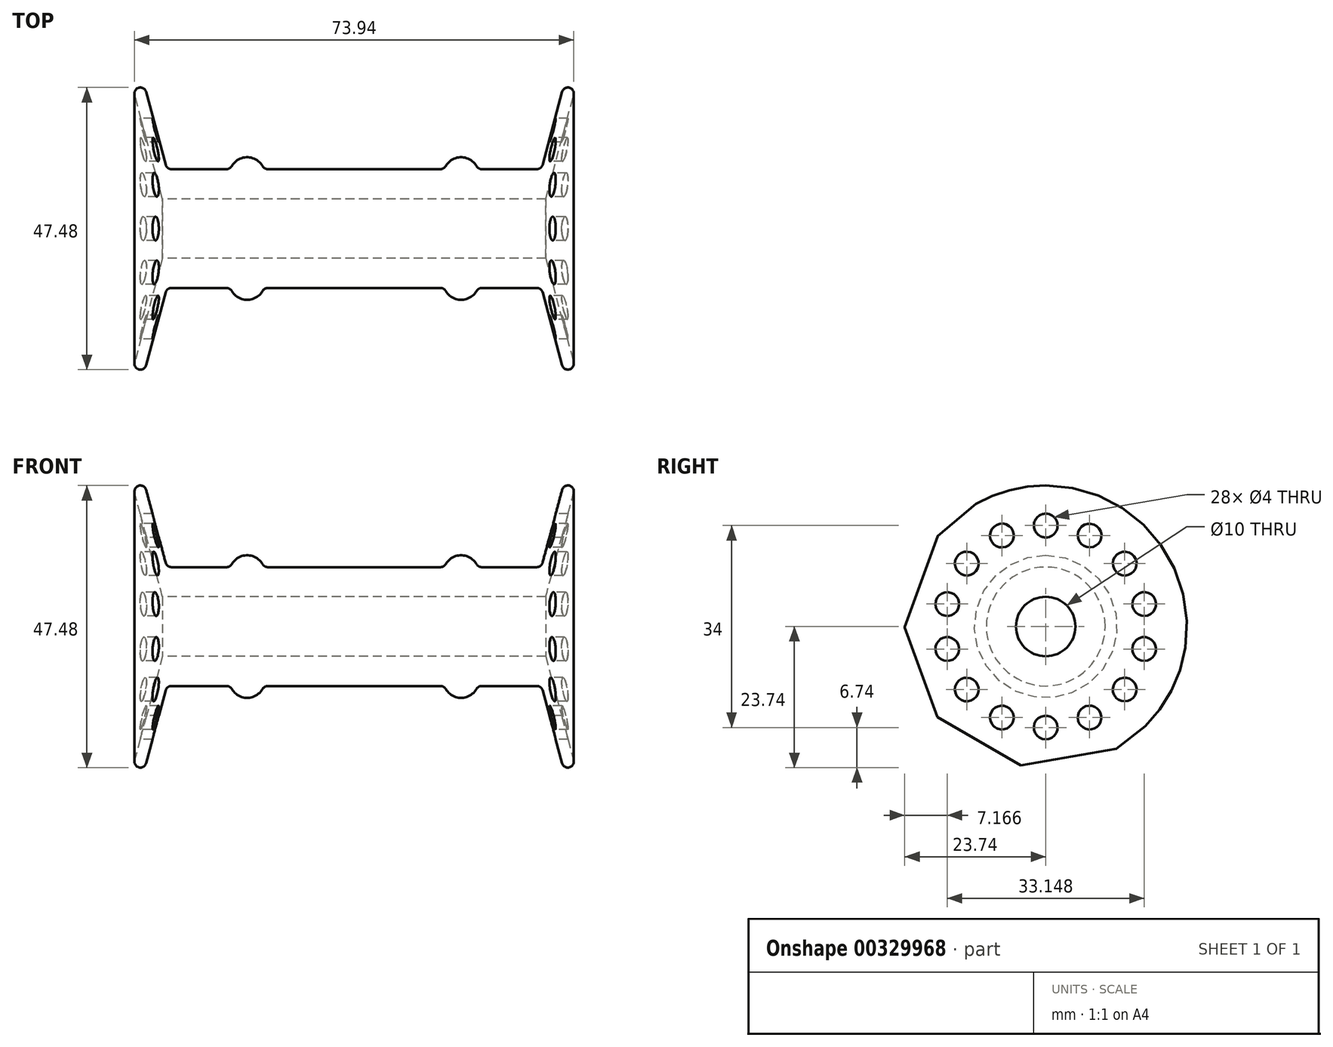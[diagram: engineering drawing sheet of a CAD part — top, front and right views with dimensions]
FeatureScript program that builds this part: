
annotation { "Feature Type Name" : "Feature", "Feature Type Description" : "" }
export const myFeature = defineFeature(function(context is Context, id is Id, definition is map)
    precondition{}
    {
        {
            var Q0;
            Q0=qCreatedBy(makeId("Front.planeOp"),FACE);
            var sketch = newSketch(context, id + "F0", { "sketchPlane" : qUnion([Q0])});
            skLineSegment(sketch, "E0", {"start": v(-32.25, 0) * mm, "end": v(32.25, 0) * mm});
            skLineSegment(sketch, "E1", {"start": v(-30.75, 5) * mm, "end": v(-21.46, 5) * mm});
            skLineSegment(sketch, "E2", {"start": v(-31.72, 5.74) * mm, "end": v(-35, 18) * mm});
            skLineSegment(sketch, "E3", {"start": v(0, 28.63) * mm, "end": v(0, 5) * mm});
            skArc(sketch, "E4", {"start": v(-15.4, 5.5) * mm, "mid": v(-18, 7) * mm, "end": v(-20.6, 5.5) * mm});
            skLineSegment(sketch, "E5.trimOffspring", {"start": v(-14.54, 5) * mm, "end": v(0, 5) * mm});
            skPoint(sketch, "E6.visualSharp", {"position": v(-20.83, 5) * mm});
            skArc(sketch, "E6.filletArc", {"start": v(-21.46, 5) * mm, "mid": v(-20.96, 5.13) * mm, "end": v(-20.6, 5.5) * mm});
            skPoint(sketch, "E7.visualSharp", {"position": v(-15.17, 5) * mm});
            skArc(sketch, "E7.filletArc", {"start": v(-15.4, 5.5) * mm, "mid": v(-15.04, 5.13) * mm, "end": v(-14.54, 5) * mm});
            skPoint(sketch, "E8.visualSharp", {"position": v(-31.52, 5) * mm});
            skArc(sketch, "E8.filletArc", {"start": v(-31.72, 5.74) * mm, "mid": v(-31.36, 5.2) * mm, "end": v(-30.75, 5) * mm});
            skArc(sketch, "E9.MirrorCS", {"start": v(15.4, 5.5) * mm, "mid": v(15.04, 5.13) * mm, "end": v(14.54, 5) * mm});
            skArc(sketch, "E10.MirrorCS", {"start": v(31.72, 5.74) * mm, "mid": v(31.36, 5.2) * mm, "end": v(30.75, 5) * mm});
            skArc(sketch, "E11.MirrorCS", {"start": v(21.46, 5) * mm, "mid": v(20.96, 5.13) * mm, "end": v(20.6, 5.5) * mm});
            skPoint(sketch, "E12.MirrorP", {"position": v(31.52, 5) * mm});
            skPoint(sketch, "E13.MirrorP", {"position": v(15.17, 5) * mm});
            skLineSegment(sketch, "E14.MirrorCS", {"start": v(30.75, 5) * mm, "end": v(21.46, 5) * mm});
            skLineSegment(sketch, "E15.MirrorCS", {"start": v(14.54, 5) * mm, "end": v(0, 5) * mm});
            skLineSegment(sketch, "E16.MirrorCS", {"start": v(31.72, 5.74) * mm, "end": v(35, 18) * mm});
            skPoint(sketch, "E17.MirrorP", {"position": v(20.83, 5) * mm});
            skArc(sketch, "E18.MirrorCS", {"start": v(15.4, 5.5) * mm, "mid": v(18, 7) * mm, "end": v(20.6, 5.5) * mm});
            skLineSegment(sketch, "E19.0", {"start": v(-32.25, 0) * mm, "end": v(-36.93, 17.48) * mm});
            skArc(sketch, "E20", {"start": v(-35, 18) * mm, "mid": v(-36.22, 18.7) * mm, "end": v(-36.93, 17.48) * mm});
            skPoint(sketch, "E21.orphan", {"position": v(-32.25, 0) * mm});
            skArc(sketch, "E22.MirrorCS", {"start": v(35, 18) * mm, "mid": v(36.22, 18.7) * mm, "end": v(36.93, 17.48) * mm});
            skLineSegment(sketch, "E23.MirrorCS", {"start": v(32.25, 0) * mm, "end": v(36.93, 17.48) * mm});
            skLineSegment(sketch, "E24", {"start": v(-32.84, -5) * mm, "end": v(39.42, -5) * mm});
            skSolve(sketch);
        }
        {
            var Q0;
            Q0 = qSketchRegion(id + "F0", true);
            var Q1;
            Q1=sQuery(id+"F0.wireOp",EDGE,"E24");
            revolve(context, id + "F1", {"entities" : qUnion([Q0]), "axis" : qUnion([Q1]), "revolveType" : RevolveType.FULL});
        }
        {
            var Q0;
            Q0=qCreatedBy(makeId("Right.planeOp"),FACE);
            var sketch = newSketch(context, id + "F2", { "sketchPlane" : qUnion([Q0])});
            skCircle(sketch, "E25", {"center": v(0, 12) * mm, "radius": 2 * mm});
            skLineSegment(sketch, "E26", {"start": v(0, 0) * mm, "end": v(0, -10) * mm});
            skLineSegment(sketch, "E27", {"start": v(-5, -5) * mm, "end": v(5, -5) * mm});
            skPoint(sketch, "E28", {"position": v(0, -5) * mm});
            skCircle(sketch, "E29.1.0", {"center": v(-7.38, 10.32) * mm, "radius": 2 * mm});
            skCircle(sketch, "E29.2.0", {"center": v(-13.3, 5.6) * mm, "radius": 2 * mm});
            skCircle(sketch, "E29.3.0", {"center": v(-16.57, -1.22) * mm, "radius": 2 * mm});
            skCircle(sketch, "E29.4.0", {"center": v(-16.57, -8.78) * mm, "radius": 2 * mm});
            skCircle(sketch, "E29.5.0", {"center": v(-13.3, -15.6) * mm, "radius": 2 * mm});
            skCircle(sketch, "E29.6.0", {"center": v(-7.38, -20.32) * mm, "radius": 2 * mm});
            skCircle(sketch, "E29.7.0", {"center": v(0, -22) * mm, "radius": 2 * mm});
            skCircle(sketch, "E29.8.0", {"center": v(7.38, -20.32) * mm, "radius": 2 * mm});
            skCircle(sketch, "E29.9.0", {"center": v(13.3, -15.6) * mm, "radius": 2 * mm});
            skCircle(sketch, "E29.10.0", {"center": v(16.57, -8.78) * mm, "radius": 2 * mm});
            skCircle(sketch, "E29.11.0", {"center": v(16.57, -1.22) * mm, "radius": 2 * mm});
            skCircle(sketch, "E29.12.0", {"center": v(13.3, 5.6) * mm, "radius": 2 * mm});
            skCircle(sketch, "E29.13.0", {"center": v(7.38, 10.32) * mm, "radius": 2 * mm});
            skSolve(sketch);
        }
        {
            var Q0;
            Q0 = qSketchRegion(id + "F2", true);
            extrude(context, id + "F3", {"entities" : qUnion([Q0]), "operationType" : NewBodyOperationType.REMOVE, "depth" : 100 * mm, "symmetric" : true});
        }
    });
